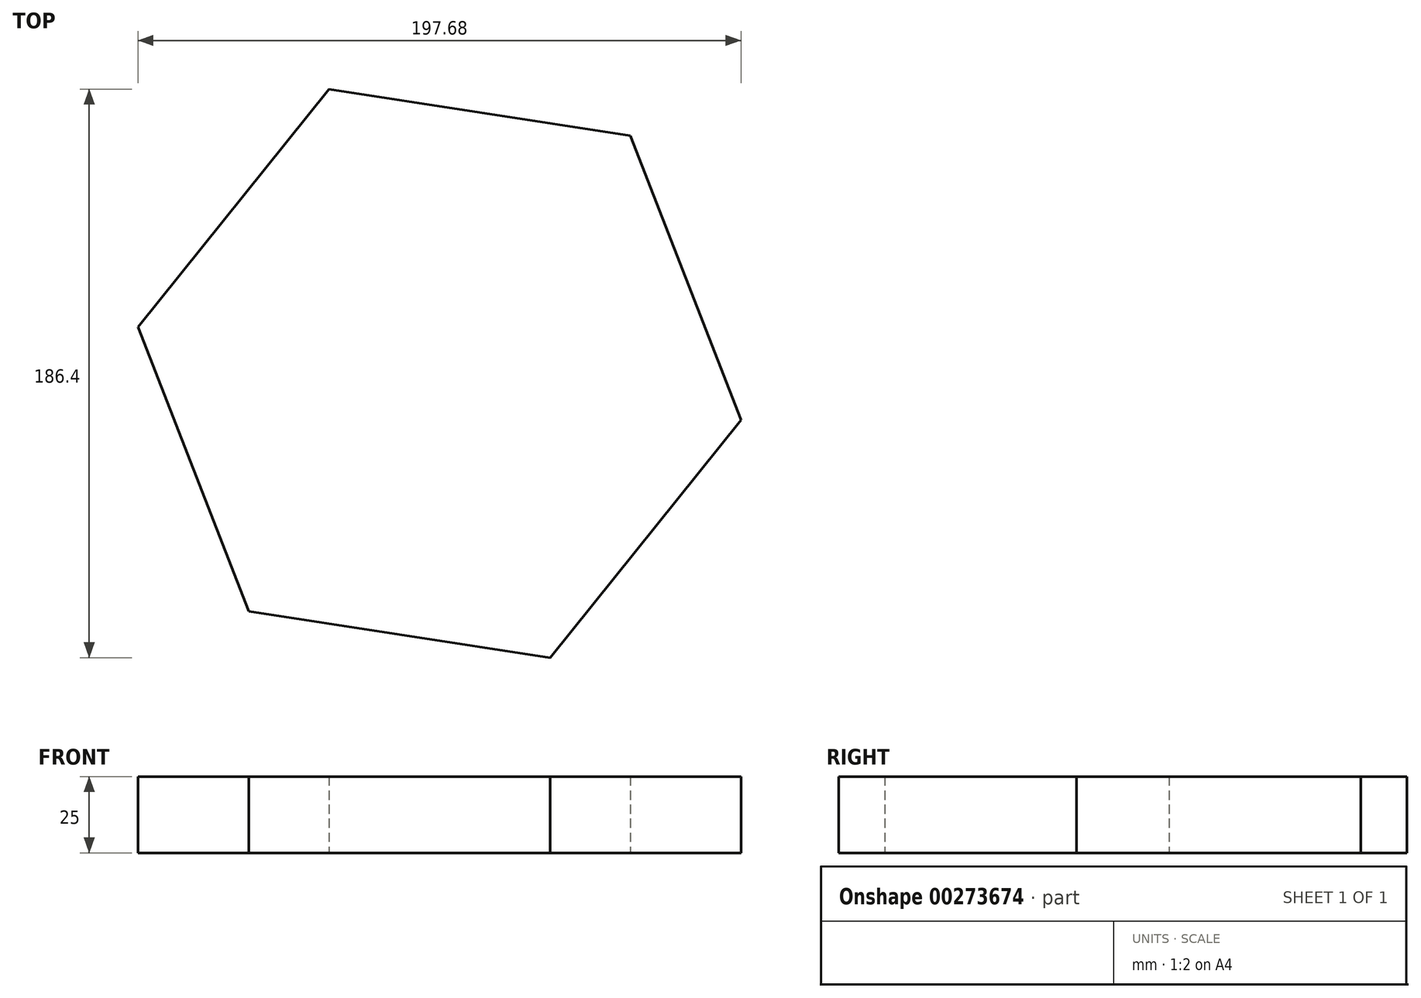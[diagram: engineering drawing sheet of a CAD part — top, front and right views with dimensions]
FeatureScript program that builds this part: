
annotation { "Feature Type Name" : "Feature", "Feature Type Description" : "" }
export const myFeature = defineFeature(function(context is Context, id is Id, definition is map)
    precondition{}
    {
        {
            var Q0;
            Q0=qCreatedBy(makeId("Top.planeOp"),FACE);
            var sketch = newSketch(context, id + "F0", { "sketchPlane" : qUnion([Q0])});
            skCircle(sketch, "E0.cCircle", {"center": v(0, 0) * mm, "radius": 86.6 * mm, "construction": true});
            skLineSegment(sketch, "E0.0", {"start": v(-62.59, -78) * mm, "end": v(-98.84, 15.2) * mm});
            skLineSegment(sketch, "E0.1", {"start": v(-98.84, 15.2) * mm, "end": v(-36.25, 93.2) * mm});
            skLineSegment(sketch, "E0.2", {"start": v(-36.25, 93.2) * mm, "end": v(62.59, 78) * mm});
            skLineSegment(sketch, "E0.3", {"start": v(62.59, 78) * mm, "end": v(98.84, -15.2) * mm});
            skLineSegment(sketch, "E0.4", {"start": v(98.84, -15.2) * mm, "end": v(36.25, -93.2) * mm});
            skLineSegment(sketch, "E0.5", {"start": v(36.25, -93.2) * mm, "end": v(-62.59, -78) * mm});
            skPoint(sketch, "E0.0.midPoint", {"position": v(-80.71, -31.4) * mm});
            skSolve(sketch);
        }
        {
            var Q0;
            Q0=makeQuery(id+"F0.imprint","IMPRINT",FACE,{"disambiguationData":[TD([[makeQuery(id+"F0.imprint","IMPRINT",EDGE,{"derivedFrom":sQuery(id+"F0.wireOp",EDGE,"E0.0")}),-1.0]])]});
            extrude(context, id + "F1", {"entities" : qUnion([Q0]), "depth" : 25 * mm});
        }
    });
